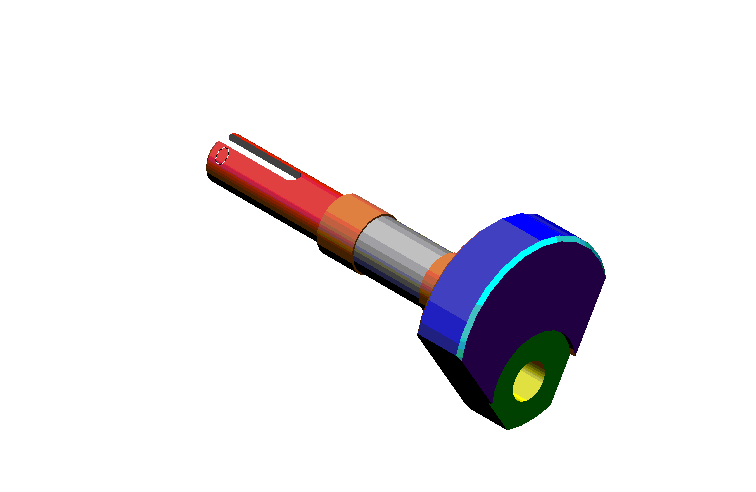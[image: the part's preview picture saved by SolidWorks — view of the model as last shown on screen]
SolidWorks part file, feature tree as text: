
SOLIDWORKS PART (.sldprt)
format: sldprt  version: not decoded by parser v0  size: 207,360 bytes
history: native  units: mm
features: sketch x8, mirror x5, plane x3, chamfer x2, material x1, revolve x1, cut_extrude x1, hole x1, thread x1 + 1 further entry (+8 scaffold rows collapsed)
feature tree (32):
  scaffold x8  (default folders/planes/origin — collapsed)
  material  "Matériau <non spécifié>"
  "Corps de surface"
  plane  "face"
  plane  "dessus"
  plane  "profil"
  sketch  "Esquisse1"  dims[c1.D12=~5.29661mm c1.D10=8.0mm c1.D1=6.0mm c1.D2=37.0mm c1.D3=7.5mm c1.D4=11.0mm c1.D5=7.0mm c1.D6=21.0mm c1.D7=11.0mm c1.D8=16.0mm c1.D9=3.5mm c2.D10=11.5mm c2.D9=9.5mm c2.D8=7.5mm c3.D10=3.5mm c3.D11=11.5mm c3.D12=3.5mm c3.D13=24.0mm c3.D14=14.0mm c3.D5=7.0mm]
  revolve  "Base-Révolution"  Angle=360deg
  chamfer  "Chanfrein1"  Distance=1mm Angle=45deg
  chamfer  "Chanfrein2"  Distance=1mm Angle=45deg
  sketch  "Esquisse2"  dims[c1.D1=48.0mm c1.D2=~32.382196mm c2.D2=60.0deg c2.D3=20.0mm]
  cut_extrude  "Enlèv. mat.-Extru.2"  [1 undecoded]
  mirror  "Symétrie1"
  sketch  "Esquisse3"  dims[D2=26.0mm D1=13.0mm]
  mirror  "Enlèv. mat.-Extru.3"
  sketch  "Esquisse4"  dims[D1=10.0mm]
  mirror  "Enlèv. mat.-Extru.4"
  sketch  "Esquisse5"  dims[D1=4.0mm D2=2.0mm D3=3.5mm]
  mirror  "Enlèv. mat.-Extru.5"
  sketch  "Esquisse18"  dims[c1.D1=4.0mm c1.D2=4.0mm c2.D1=22.0mm]
  mirror  "Enlèv. mat.-Extru.6"
  hole  "Perçage5"  Diameter=3.3mm Depth=15.5mm
  sketch  "Esquisse17"
  sketch  "Esquisse16"  dims[hole-wizard template sketch: 46 standard entries collapsed; hole parameters kept: c15.Diamètre du perçage=3.3mm c15.Profondeur du perçage=15.5mm c15.D3=~14.816244mm c15.Angle de pointe=118.0deg]
  thread  "Représentation de filetage8"  Diameter=12mm  [1 undecoded]
decode coverage: 12 of 19 modeling features carry decoded parameters; 1 rows unclassified (native names shown)
note: ~ marks probable driven/reference dimensions
note: 2 parameter values undecoded
note: suppression state not decoded; provenance and decode notes live in map.json
